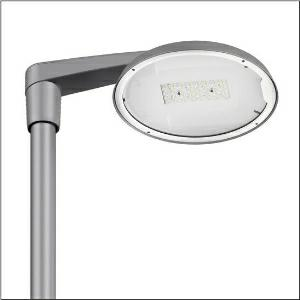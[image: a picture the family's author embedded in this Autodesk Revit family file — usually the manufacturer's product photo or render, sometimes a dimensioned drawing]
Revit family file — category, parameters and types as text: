
# Revit family: dl_r__50_iq_mini___st0_5a_5xa248b31f08fe_5b8c
name_source: partatom
category: Lighting Fixtures
units: mm (PartAtom-declared; Revit-internal decimal feet)

## family parameters
Cut with Voids When Loaded = No
Host = Face
Light Source = No
Part Type = Normal
Room Calculation Point = No
Round Connector Dimension = Use Diameter
Shared = No

## types (1)
- --- (1 x LED, 2700 lm, 16.3 W, 3000K)
    Apparent Load = 16 VA
    CIE Flux Codes = 41 75 97 100 100
    Color Rendering = 70
    Color Temperature = 3000K
    Default Elevation = 1800 mm
    Description = DL® 50 iQ mini, mast luminaire, primary light control with lens, of PMMA, primary optical cover: cover, of toughened safety glass, transparent, light distribution: ST0.5a, light emission: direct distribution, primary light characteristic: asymmetric, installation type: side-entry, post-top, LED, High Power LED, rated luminous flux: 2.700lm, luminous efficacy: 166lm/W, light colour: 730, colour temperature: 3000K, control gear: iQ Street-Remote, control: optimised constant luminous flux control (CLO 2.0), Desk-Remote (wireless, voltage-free reading and setting of iQ features in the workshop via application-optimized NFC function/RFID function), Light-Fading, Smart-Wire, Night-Set, Lumen-Switch, Temp-Guard, Auto-Match, Street-Remote, mains connection: 230..240V, AC, 50/60Hz, connection cable pre-assembled, cable length: 6,5m, start of lifetime: 16W, end of service life: 17W, reduction: 8W, luminaire housing, of diecast aluminium, powder-coated, Siteco® metallic grey (DB 702S), inclination adjustable: 0°, 5°, 10° (post-top) | 0°, -5°, -10°, -15° (side-entry), please order mast post-top element or mast side-entry element separately, diameter: 500mm, height: 115mm, post-top: for spigot size d x l = 76 x 100mm; with reducer (optional accessory) 60 x 100mm | side-entry: for spigot size d x l = 60 x 100mm; with reducer (optional accessory) 42 x 100mm, mounting height: 4..6m, protection rating (complete): IP66, insulation class (complete): insulation class II (safety insulation), certification: CE, ENEC, ENEC+, VDE, impact resistance: IK08, permissible operating ambient temperature for outdoor applications: -25..+40°C, standard-compliant lighting for roads and squares, packaging unit: 1 piece

Light Distribution: ST0.5a
    Height = 115 mm
    Lamp = 1 x LED
    Lamp Light Flux = 2700 lm
    Lamp Power = 16.3 W
    Lamp count = 1
    Length = 500 mm
    Luminous efficacy = 166 lm/W
    Manufacturer = Siteco
    ModVariant = No
    Model = 5XA248B31F08FE
    Number of Poles = 1
    OnlyDefault = Yes
    Power Factor = 1
    Product Name = DL® 50 iQ mini | ST0.5a
    Product group = mast luminaire | pylon top
    ProductGroupID = 6100
    Protection Class = Protection class II
    Protection Degree = IP 66
    RLX_Detail_Level = 1
    RLX_Emergency_Light_Flux = 0 lm
    RLX_Emergency_Type = 0
    RLX_Emergency_Type_DB = No
    RlxData = <blob elided: 126649 chars, md5=f1f9522c>
    Socket = socket
    Standby Power = 0 W
    System Light Flux = 2700 lm
    System Power = 16 W
    Type Comments = factory setting: luminous flux: 100 % | dim-lin: 254 | 333 mA
    Type Image = l_1251794.jpg
    URL = http://relux.com
    VarID = @adj_160909
    Voltage = 0 V
    Weight = 0.00 kg
    Width = 0 mm  [stored 0 ft]

note: [stored X ft] marks values corroborated as IEEE doubles in the binary element streams (Revit-internal decimal feet)

## geometry (parser evidence)
native form markers: Blend x4, Sweep x10
no freeform markers — native parametric forms only
